FCSTD DOCUMENT  (FreeCAD 1.0R39319 (Git))
Label: Assy_IMX296
License: All rights reserved
LicenseURL: https://en.wikipedia.org/wiki/All_rights_reserved
objects: App::DocumentObjectGroup×3, App::Link×2, PartDesign::CoordinateSystem×1, App::FeaturePython×1, App::Part×1
note: 1 computed .brp shape members not serialized (recipe doc carries the construction recipe); baked Part::Feature solids carry a one-line shape summary decoded from their .brp
EXTERNAL_REF file=../../Part/Purchase/IMX296 With CS.FCStd obj=LCS_1
EXTERNAL_REF file=../../Part/Purchase/IMX296 With CS.FCStd obj=Document
EXTERNAL_REF file=../../Part/Purchase/IMX296 With CS.FCStd obj=Lens_att
EXTERNAL_REF file=../../Part/Purchase/Lens_PT361060M3MP12.FCStd obj=LCS_1
EXTERNAL_REF file=../../Part/Purchase/Lens_PT361060M3MP12.FCStd obj=Part

FEATURE [App::DocumentObjectGroup] Parts
FEATURE [PartDesign::CoordinateSystem] LCS_Origin
  AttacherType = Attacher::AttachEngine3D
  AttachmentSupport = -> [X_Axis]
  MapMode = 2
FEATURE [App::DocumentObjectGroup] Constraints
FEATURE [App::FeaturePython] Variables  # WARN: FeaturePython — macro-defined, semantics opaque (R4)
  Type = App::PropertyContainer
FEATURE [App::DocumentObjectGroup] Configurations
FEATURE [App::Link] Document
  AttachedBy = #LCS_1
  AttachedTo = Parent Assembly#LCS_Origin
  LinkPlacement = pos=(17,-17,2.5) rot=(-0.707107,-0.707107,0;3.14159rad)
  LinkedObject = -> <external ../../Part/Purchase/IMX296 With CS.FCStd>#Document
  Placement = pos=(17,-17,2.5) rot=(-0.707107,-0.707107,0;3.14159rad)
  SolverId = Asm4EE
  expr: Placement = LCS_Origin.Placement * AttachmentOffset * IMX296_With_CS#LCS_1.Placement ^ -1
FEATURE [App::Link] Lens_PT361060M3MP12
  AttachedBy = #LCS_1
  AttachedTo = Document#Lens_att
  AttachmentOffset = pos=(0,0,0) rot=(0,1,0;3.14159rad)
  LinkPlacement = pos=(17,-17,-5.7) rot=(0.707107,0.707107,0;3.14159rad)
  LinkedObject = -> <external ../../Part/Purchase/Lens_PT361060M3MP12.FCStd>#Part
  Placement = pos=(17,-17,-5.7) rot=(0.707107,0.707107,0;3.14159rad)
  SolverId = Asm4EE
  expr: Placement = Document.Placement * IMX296_With_CS#Lens_att.Placement * AttachmentOffset * Lens_PT361060M3MP12#LCS_1.Placement ^ -1
FEATURE [App::Part] Assembly  label="Assy_IMX296"
  AssemblyType = Part::Link
  Group = -> [LCS_Origin,Constraints,Variables,Configurations,Document,Lens_PT361060M3MP12]
  Origin = -> Origin
  Type = Assembly

RESOLVED EXTERNAL PARTS (link-assembly join: the EXTERNAL_REF files above that resolve inside this repo's crawl, each included once):
---- part ../../Part/Purchase/Lens_PT361060M3MP12.FCStd = doc fcstd_35e111300a33 ----
FCSTD DOCUMENT  (FreeCAD 1.0R39319 (Git))
Label: Lens_PT361060M3MP12
License: All rights reserved
LicenseURL: https://en.wikipedia.org/wiki/All_rights_reserved
objects: Sketcher::SketchObject×1, PartDesign::Revolution×1, PartDesign::Body×1, PartDesign::CoordinateSystem×1, App::Part×1
note: 7 computed .brp shape members not serialized (recipe doc carries the construction recipe); baked Part::Feature solids carry a one-line shape summary decoded from their .brp

FEATURE [Sketcher::SketchObject] Sketch
  ArcFitTolerance = 1e-06
  AttachmentSupport = -> [XZ_Plane001]
  FullyConstrained = true
  MakeInternals = false
  MapMode = 5
  Placement = pos=(0,0,0) rot=(1,0,0;1.5708rad)
  sketch-geometry (8):
    g0: LineSegment StartX=0 StartY=0 StartZ=0 EndX=12.8 EndY=0 EndZ=0
    g1: LineSegment StartX=12.8 StartY=0 StartZ=0 EndX=12.8 EndY=5 EndZ=0
    g2: LineSegment StartX=12.8 StartY=5 StartZ=0 EndX=15 EndY=5 EndZ=0
    g3: LineSegment StartX=15 StartY=5 StartZ=0 EndX=15 EndY=34 EndZ=0
    g4: LineSegment StartX=15 StartY=34 StartZ=0 EndX=13 EndY=34 EndZ=0
    g5: LineSegment StartX=13 StartY=34 StartZ=0 EndX=13 EndY=31 EndZ=0
    g6: LineSegment StartX=13 StartY=31 StartZ=0 EndX=0 EndY=31 EndZ=0
    g7: LineSegment StartX=0 StartY=31 StartZ=0 EndX=0 EndY=0 EndZ=0
  constraints (24):
    c: PointOnObject(g0,g-2)
    c: Horizontal(g0)
    c: Coincident(g0,g1)
    c: Vertical(g1)
    c: Coincident(g1,g2)
    c: Horizontal(g2)
    c: Coincident(g2,g3)
    c: Vertical(g3)
    c: Coincident(g3,g4)
    c: Coincident(g4,g5)
    c: Vertical(g5)
    c: Coincident(g5,g6)
    c: Horizontal(g6)
    c: Coincident(g6,g7)
    c: Coincident(g7,g0)
    c: Vertical(g7)
    c: Distance(g7,g1) = 12.8
    c: Distance(g7,g3) = 15
    c: Horizontal(g4)
    c: Distance(g0,g4) = 34
    c: Distance(g0,g2) = 5
    c: Distance(g-2,g5) = 13
    c: Distance(g4,g6) = 3
    c: PointOnObject(g0,g-1)
FEATURE [PartDesign::Revolution] Revolution
  Angle = 360
  Angle2 = 60
  Axis = (0,2e-16,1)
  Base = (0,0,0)
  Placement = pos=(0,0,0) rot=(1,0,0;1.5708rad)
  Profile = -> Sketch
  ReferenceAxis = -> Sketch [V_Axis]
  Refine = true
  Reversed = true
  Suppressed = false
  Type = 0
FEATURE [PartDesign::Body] Body  label="Lens_PT361060M3MP1201"
  AllowCompound = false
  Group = -> [Sketch,Revolution]
  Origin = -> Origin001
  Tip = -> Revolution
FEATURE [PartDesign::CoordinateSystem] LCS_1
  AttacherType = Attacher::AttachEngine3D
  AttachmentSupport = -> [Revolution]
  MapMode = 11
  Placement = pos=(-1.8e-15,2.2e-15,5) rot=(0.707107,-0.707107,0;3.14159rad)
FEATURE [App::Part] Part  label="Lens_PT361060M3MP12"
  Group = -> [Body,LCS_1]
  Origin = -> Origin
